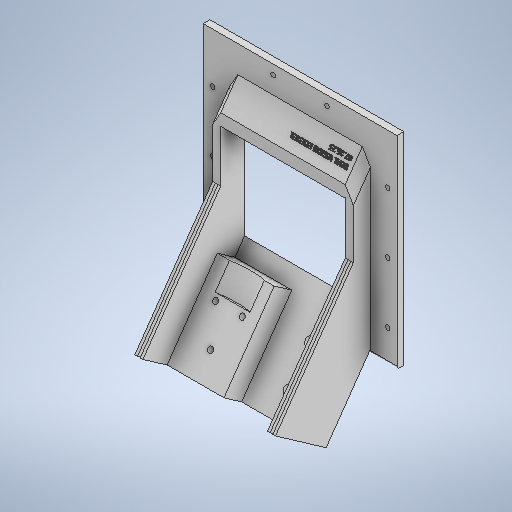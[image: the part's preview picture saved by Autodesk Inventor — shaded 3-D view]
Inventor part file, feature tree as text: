
AUTODESK INVENTOR PART (.ipt)
format: ipt  version: 2025.2 (Build 292293000, 293)  size: 1,312,768 bytes
history: native  units: in
note: dims shown in document units (in); Inventor stores cm internally (conversion verified against a paired STEP export)
features: sketch x35, extrude x30, plane x5, projected_geometry x3, move_body x1, chamfer x1, fillet x1, hole x1
ambient origin geometry x8: Origin, YZ Plane, XZ Plane, XY Plane, X Axis, Y Axis, Z Axis, Center Point
bodies: Solid1 (feature_tree)
feature tree (77):
  extrude  "Extrusion1"  Depth=0.1969in TaperAngle=0.0deg
  move_body  "Move Body1"
  plane  "Work Plane1"
  sketch  "Sketch5"  dims[d5=1.7717in d6=1.7717in d7=1.7717in d8=1.7717in d9=0.8108in d10=90.0deg d11=0.0787in d12=0.3701in d13=0.4252in d14=0.1362in d15=-0.0984in d16=-0.0591in d17=0.0in]
  plane  "Work Plane2"
  extrude  "Extrusion4"  TaperAngle=0.0deg  [1 undecoded]
  extrude  "Extrusion6"  Depth=0.2405in
  extrude  "Extrusion8"  Depth=2.5591in TaperAngle=0.0deg
  chamfer  "Chamfer1"  [1 undecoded]
  extrude  "Extrusion11"  Depth=0.2362in
  plane  "Work Plane3"
  extrude  "Extrusion13"  Depth=0.1969in TaperAngle=0.0deg
  plane  "Work Plane4"
  plane  "Work Plane6"
  extrude  "Extrusion21"  Depth=0.5027in
  extrude  "Extrusion22"  Depth=0.5027in
  extrude  "Extrusion25"  Depth=1.1811in TaperAngle=0.0deg
  extrude  "Extrusion26"  Depth=0.1969in
  sketch  "Sketch33"  dims[d100=3.6403in d101=2.7717in]
  extrude  "Extrusion27"  Depth=0.2362in TaperAngle=0.0deg
  extrude  "Extrusion28"  Depth=3.6403in
  sketch  "Sketch36"  dims[d124=0.9712in d125=0.0in d126=0.5906in d127=0.0in]
  extrude  "Extrusion29"  Depth=0.6299in TaperAngle=0.0deg
  extrude  "Extrusion30"  Depth=0.1575in
  extrude  "Extrusion31"  Depth=0.5906in TaperAngle=0.0deg
  sketch  "Sketch39"  dims[d139=0.1181in d140=0.0in d141=0.6299in]
  extrude  "Extrusion32"  Depth=11.3469in TaperAngle=0.0deg
  fillet  "Fillet1"  Radius=0.4331in
  extrude  "Extrusion33"  Depth=0.4331in
  extrude  "Extrusion34"  Depth=0.1181in
  extrude  "Extrusion35"  Depth=0.0787in
  sketch  "Sketch45"  dims[d164=0.1181in d165=0.0in d168=0.5906in d169=0.0in]
  extrude  "Extrusion37"  TaperAngle=0.0deg  [1 undecoded]
  extrude  "Extrusion38"  Depth=0.1181in TaperAngle=0.0deg
  extrude  "Extrusion40"  Depth=0.1181in TaperAngle=0.0deg
  extrude  "Extrusion41"  Depth=0.1181in TaperAngle=0.0deg
  extrude  "Extrusion43"  TaperAngle=0.0deg  [1 undecoded]
  extrude  "Extrusion44"  TaperAngle=0.0deg  [1 undecoded]
  extrude  "Extrusion46"  TaperAngle=0.0deg  [1 undecoded]
  extrude  "Extrusion47"  Depth=0.5906in
  extrude  "Extrusion48"  Depth=0.0394in TaperAngle=0.0deg
  sketch  "Sketch61"  dims[d58=0.0344in]
  extrude  "Extrusion50"  Depth=3.9671in TaperAngle=0.0deg
  extrude  "Extrusion51"  Depth=0.0197in
  sketch  "Sketch1"  dims[d1=0.5512in d2=0.1969in d3=0.0in]
  sketch  "Sketch6"  dims[d18=0.2749in d24=0.2405in]
  sketch  "Sketch8"  dims[d25=2.7559in d26=0.0in d29=2.5591in d30=0.0in d36=0.0in d37=0.0in]
  sketch  "Sketch12"  dims[d42=0.2362in d43=0.2362in]
  sketch  "Sketch15"  dims[d52=0.2362in d53=0.0787in d54=45.0deg d55=0.1969in d56=0.0in]
  sketch  "Sketch17"  dims[d59=0.5906in d60=0.0in d76=0.5027in]
  sketch  "Sketch27"  dims[d77=0.5027in d78=0.5027in]
  sketch  "Sketch28"  dims[d79=0.5027in d81=1.1811in d82=0.0in]
  sketch  "Sketch31"  dims[d83=0.0in d84=0.0in d91=0.1969in]
  sketch  "Sketch32"  dims[d94=0.2362in d95=0.0in d96=0.2362in d97=0.0in]
  sketch  "Sketch34"  dims[d112=1.9685in d113=0.6299in d114=0.0in]
  sketch  "Sketch35"  dims[d115=0.1575in d117=0.1575in d121=1.9685in d122=0.7874in d123=0.9331in]
  sketch  "Sketch37"  dims[d128=11.3469in d129=0.0in d130=11.3469in d131=0.0in d136=0.4331in]
  sketch  "Sketch38"  dims[d137=0.4331in d138=0.4331in]
  sketch  "Sketch40"  dims[d142=0.0787in d147=0.2756in]
  sketch  "Sketch41"  dims[d149=0.2756in d150=0.0in d151=0.0in]
  sketch  "Sketch42"  dims[d154=0.1181in d155=0.0in d156=0.1181in d157=0.0in]
  sketch  "Sketch44"  dims[d158=0.5906in d160=0.1181in d161=0.0in d162=0.1969in d163=0.0in]
  projected_geometry  "Projected Loop2"
  projected_geometry  "Projected Loop3"
  projected_geometry  "Projected Loop5"
  sketch  "Sketch47"  dims[d170=4.7244in d171=0.0in d174=0.0in d175=0.0in]
  sketch  "Sketch49"  dims[d176=0.7313in d177=0.0in d186=0.0in d187=0.0in]
  sketch  "Sketch50"  dims[d188=0.0in d189=0.0in d194=0.0in d195=0.0in]
  sketch  "Sketch52"  dims[d196=1.1024in d197=0.5906in]
  sketch  "Sketch53"  dims[d198=0.0394in d199=0.0in d200=0.0394in d201=0.0in]
  sketch  "Sketch56"  dims[d235=6.1063in d236=0.0in d244=3.9671in d245=0.0in]
  sketch  "Sketch58"  dims[d246=0.9963in d38=0.0197in]
  sketch  "Sketch59"  dims[d39=0.0344in d57=0.0197in]
  sketch  "Sketch63"  dims[d159=0.0344in]
  sketch  "Sketch64"  dims[d178=0.0in d179=0.0in d180=0.0in d181=0.0in d202=0.0197in d203=0.0344in]
  sketch  "Sketch2"  dims[d4=0.315in]
  hole  "Hole1"  [1 undecoded]
note: 7 required parameter values undecoded (feature->parameter linkage not recoverable at this tier; creation-order binding heuristic only, values carry confidence <= 0.55)
